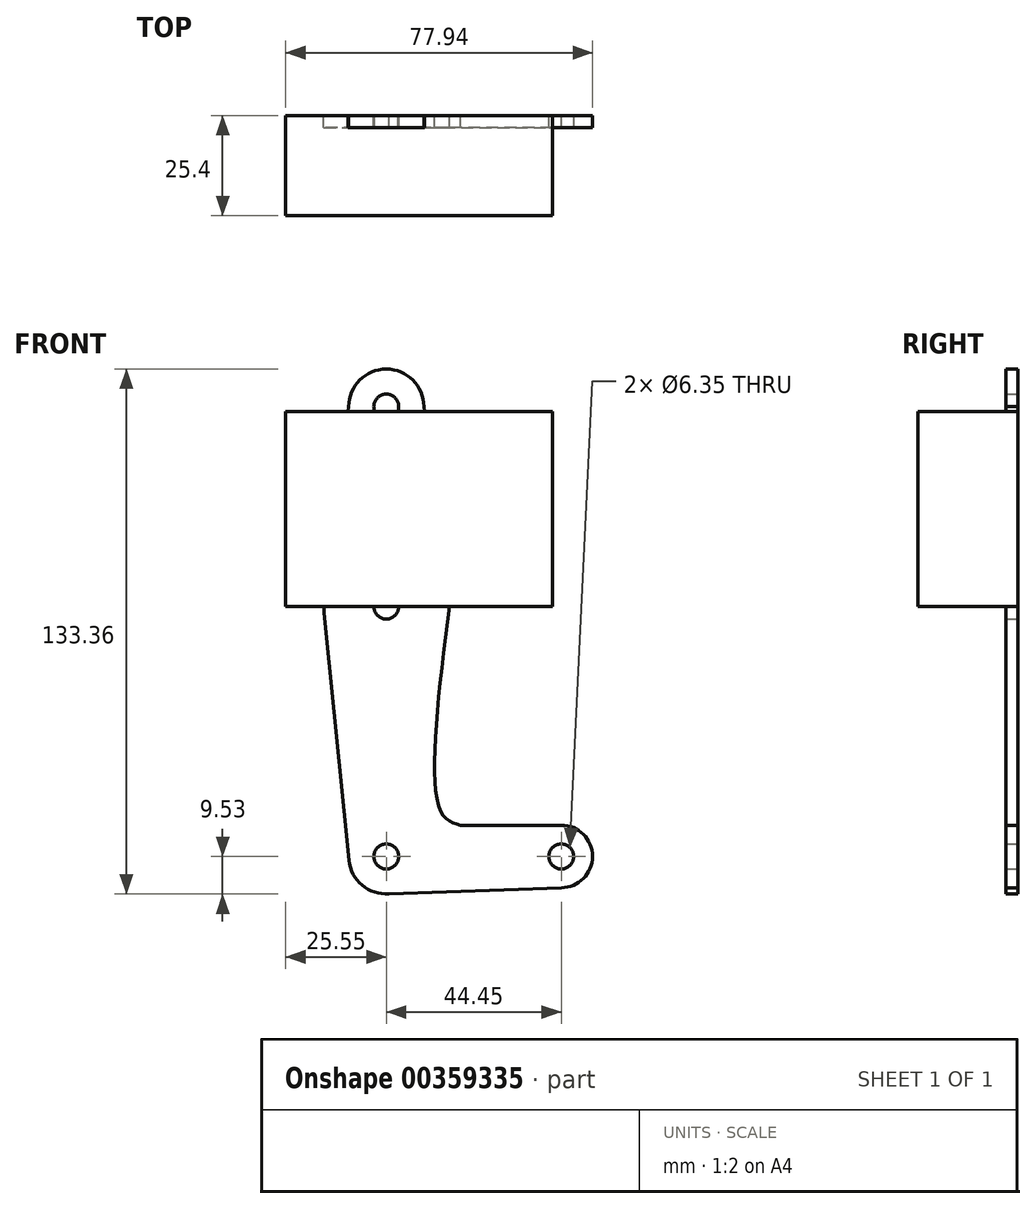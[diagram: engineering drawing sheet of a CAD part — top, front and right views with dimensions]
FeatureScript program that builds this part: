
annotation { "Feature Type Name" : "Feature", "Feature Type Description" : "" }
export const myFeature = defineFeature(function(context is Context, id is Id, definition is map)
    precondition{}
    {
        {
            var Q0;
            Q0=qCreatedBy(makeId("Front.planeOp"),FACE);
            var sketch = newSketch(context, id + "F0", { "sketchPlane" : qUnion([Q0])});
            skCircle(sketch, "E0", {"center": v(0, 0) * mm, "radius": 15.88 * mm});
            skLineSegment(sketch, "E1", {"start": v(0, 0) * mm, "end": v(0, -63.5) * mm});
            skCircle(sketch, "E2", {"center": v(0, -63.5) * mm, "radius": 9.53 * mm});
            skLineSegment(sketch, "E3", {"start": v(0, 0) * mm, "end": v(0, 50.8) * mm});
            skCircle(sketch, "E4", {"center": v(0, 50.8) * mm, "radius": 9.53 * mm});
            skCircle(sketch, "E5", {"center": v(44.45, -63.5) * mm, "radius": 7.94 * mm});
            skLineSegment(sketch, "E6", {"start": v(9.53, 50.8) * mm, "end": v(16, 0) * mm});
            skLineSegment(sketch, "E7", {"start": v(-9.53, 50.8) * mm, "end": v(-16, 0) * mm});
            skLineSegment(sketch, "E8", {"start": v(-15.8, -1.63) * mm, "end": v(-9.48, -64.45) * mm});
            skLineSegment(sketch, "E9", {"start": v(35.27, 0) * mm, "end": v(35.27, 36.53) * mm});
            skCircle(sketch, "E10", {"center": v(-1.94, 36.53) * mm, "radius": 1.59 * mm});
            skLineSegment(sketch, "E11", {"start": v(0, -73.02) * mm, "end": v(44.45, -71.44) * mm});
            skLineSegment(sketch, "E12", {"start": v(-25.67, -63.5) * mm, "end": v(-25.67, 50.8) * mm});
            skLineSegment(sketch, "E13", {"start": v(44.45, -55.56) * mm, "end": v(18.85, -55.56) * mm});
            skFitSpline(sketch, "E14", {"points": [v(18.85, -55.56) * mm, v(13.85, -52.08) * mm, v(16, 0) * mm], "startDerivative": vector(-22.5, 6.5) * mm, "endDerivative": vector(11.29, 90.83) * mm});
            skCircle(sketch, "E15", {"center": v(0, 50.8) * mm, "radius": 3.18 * mm});
            skCircle(sketch, "E16", {"center": v(44.45, -63.5) * mm, "radius": 3.18 * mm});
            skCircle(sketch, "E17", {"center": v(0, -63.5) * mm, "radius": 3.18 * mm});
            skCircle(sketch, "E18", {"center": v(0, 0) * mm, "radius": 3.18 * mm});
            skArc(sketch, "E19", {"start": v(18.85, -55.56) * mm, "mid": v(26.32, -50.31) * mm, "end": v(23.92, -41.5) * mm});
            skSolve(sketch);
        }
        {
            var Q0;
            Q0 = qSketchRegion(id + "F0", true);
            extrude(context, id + "F1", {"entities" : qUnion([Q0]), "depth" : 3.05 * mm});
        }
        {
            var Q0;
            Q0=qCreatedBy(makeId("Front.planeOp"),FACE);
            var sketch = newSketch(context, id + "F2", { "sketchPlane" : qUnion([Q0])});
            skLineSegment(sketch, "E20", {"start": v(-25.55, 49.6) * mm, "end": v(42.24, 49.6) * mm});
            skLineSegment(sketch, "E21", {"start": v(-52.14, 0) * mm, "end": v(42.24, 0) * mm});
            skLineSegment(sketch, "E22", {"start": v(42.24, 47.75) * mm, "end": v(42.24, 49.6) * mm});
            skLineSegment(sketch, "E23", {"start": v(42.24, 0) * mm, "end": v(42.24, 47.75) * mm});
            skLineSegment(sketch, "E24", {"start": v(-25.55, 49.6) * mm, "end": v(-25.55, 0) * mm});
            skSolve(sketch);
        }
        {
            var Q0;
            Q0=makeQuery(id+"F2.imprint","IMPRINT",FACE,{"disambiguationData":[TD([[makeQuery(id+"F2.imprint","IMPRINT",EDGE,{"derivedFrom":sQuery(id+"F2.wireOp",EDGE,"E20")}),-1.0]])]});
            extrude(context, id + "F3", {"entities" : qUnion([Q0]), "operationType" : NewBodyOperationType.ADD, "depth" : 25.4 * mm});
        }
    });
